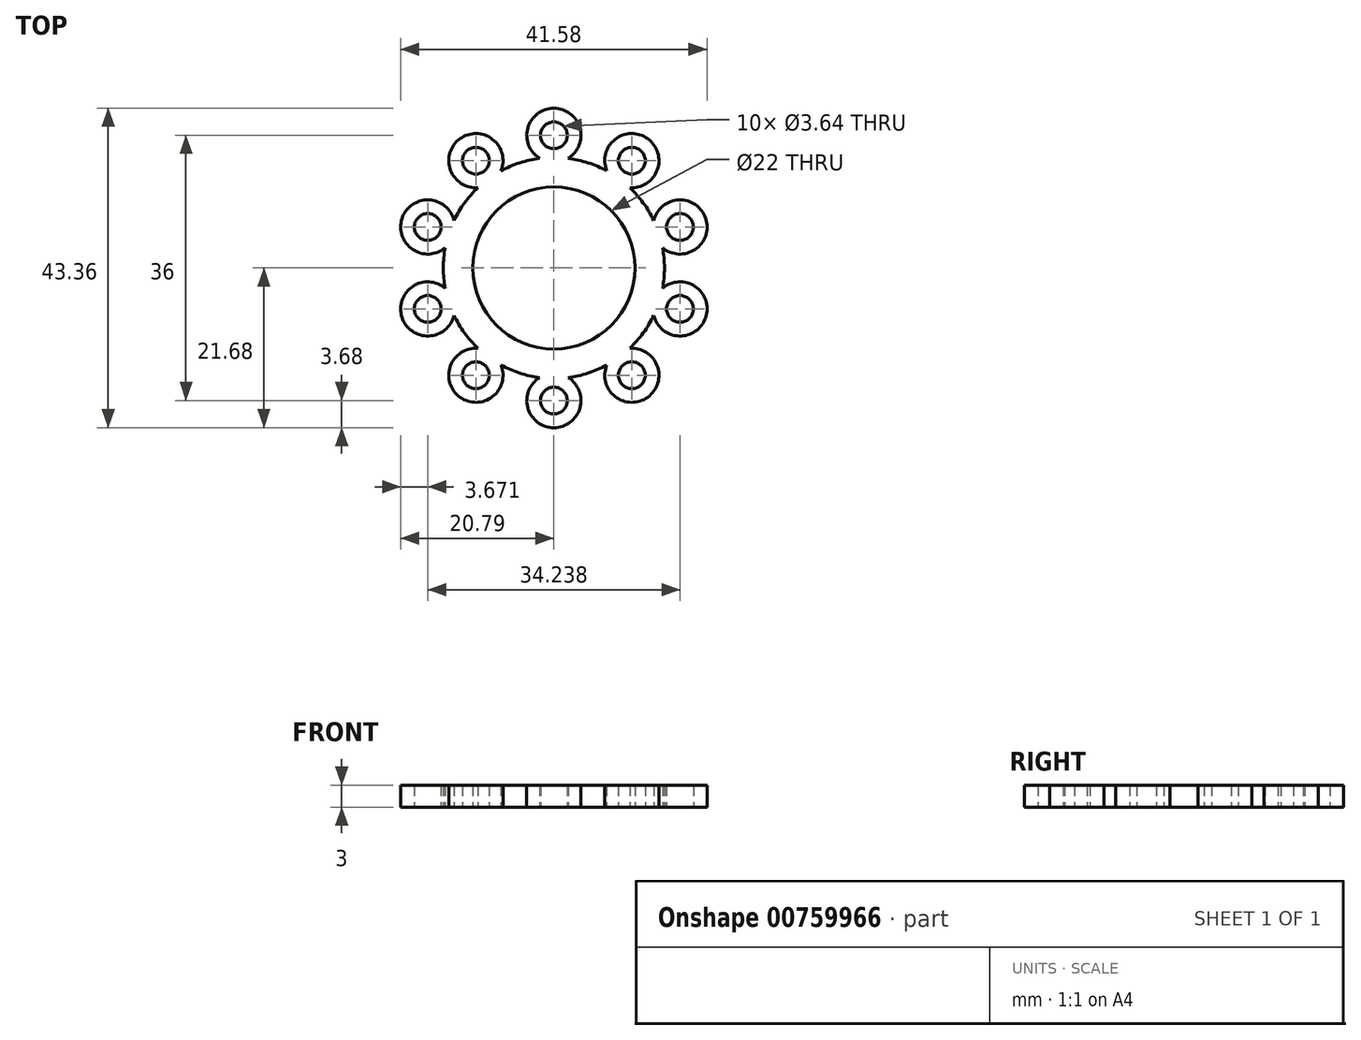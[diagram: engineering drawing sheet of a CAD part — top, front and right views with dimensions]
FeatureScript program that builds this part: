
annotation { "Feature Type Name" : "Feature", "Feature Type Description" : "" }
export const myFeature = defineFeature(function(context is Context, id is Id, definition is map)
    precondition{}
    {
        {
            var Q0;
            Q0=qCreatedBy(makeId("Top.planeOp"),FACE);
            var sketch = newSketch(context, id + "F0", { "sketchPlane" : qUnion([Q0])});
            skArc(sketch, "E0", {"start": v(3.4, 10.46) * mm, "mid": v(0, 11) * mm, "end": v(-3.4, 10.46) * mm});
            skArc(sketch, "E1", {"start": v(4.64, 14.27) * mm, "mid": v(3.3, 14.63) * mm, "end": v(1.93, 14.87) * mm});
            skLineSegment(sketch, "E2", {"start": v(0, 0) * mm, "end": v(0, 11) * mm});
            skCircle(sketch, "E3", {"center": v(0, 18) * mm, "radius": 1.82 * mm});
            skArc(sketch, "E4", {"start": v(1.93, 14.87) * mm, "mid": v(0, 21.68) * mm, "end": v(-1.93, 14.87) * mm});
            skLineSegment(sketch, "E5.trimOffspring", {"start": v(0, 14.32) * mm, "end": v(0, 18) * mm});
            skArc(sketch, "E6.trimOffspring", {"start": v(-1.93, 14.87) * mm, "mid": v(-3.3, 14.63) * mm, "end": v(-4.64, 14.27) * mm});
            skArc(sketch, "E7.1.0", {"start": v(-7.18, 13.17) * mm, "mid": v(-12.74, 17.54) * mm, "end": v(-10.3, 10.9) * mm});
            skCircle(sketch, "E7.1.1", {"center": v(-10.58, 14.56) * mm, "radius": 1.82 * mm});
            skArc(sketch, "E7.1.2", {"start": v(-4.64, 14.27) * mm, "mid": v(-5.93, 13.78) * mm, "end": v(-7.18, 13.17) * mm});
            skArc(sketch, "E7.1.3", {"start": v(-3.4, 10.46) * mm, "mid": v(-6.47, 8.9) * mm, "end": v(-8.9, 6.47) * mm});
            skArc(sketch, "E7.1.4", {"start": v(-10.3, 10.9) * mm, "mid": v(-11.27, 9.9) * mm, "end": v(-12.14, 8.82) * mm});
            skArc(sketch, "E7.2.0", {"start": v(-13.55, 6.44) * mm, "mid": v(-20.61, 6.7) * mm, "end": v(-14.74, 2.76) * mm});
            skCircle(sketch, "E7.2.1", {"center": v(-17.12, 5.56) * mm, "radius": 1.82 * mm});
            skArc(sketch, "E7.2.2", {"start": v(-12.14, 8.82) * mm, "mid": v(-12.9, 7.66) * mm, "end": v(-13.55, 6.44) * mm});
            skArc(sketch, "E7.2.3", {"start": v(-8.9, 6.47) * mm, "mid": v(-10.46, 3.4) * mm, "end": v(-11, 0) * mm});
            skArc(sketch, "E7.2.4", {"start": v(-14.74, 2.76) * mm, "mid": v(-14.94, 1.38) * mm, "end": v(-15, 0) * mm});
            skArc(sketch, "E7.3.0", {"start": v(-14.74, -2.76) * mm, "mid": v(-20.61, -6.7) * mm, "end": v(-13.55, -6.44) * mm});
            skCircle(sketch, "E7.3.1", {"center": v(-17.12, -5.56) * mm, "radius": 1.82 * mm});
            skArc(sketch, "E7.3.2", {"start": v(-15, 0) * mm, "mid": v(-14.94, -1.38) * mm, "end": v(-14.74, -2.76) * mm});
            skArc(sketch, "E7.3.3", {"start": v(-11, 0) * mm, "mid": v(-10.46, -3.4) * mm, "end": v(-8.9, -6.47) * mm});
            skArc(sketch, "E7.3.4", {"start": v(-13.55, -6.44) * mm, "mid": v(-12.9, -7.66) * mm, "end": v(-12.14, -8.82) * mm});
            skArc(sketch, "E7.4.0", {"start": v(-10.3, -10.9) * mm, "mid": v(-12.74, -17.54) * mm, "end": v(-7.18, -13.17) * mm});
            skCircle(sketch, "E7.4.1", {"center": v(-10.58, -14.56) * mm, "radius": 1.82 * mm});
            skArc(sketch, "E7.4.2", {"start": v(-12.14, -8.82) * mm, "mid": v(-11.27, -9.9) * mm, "end": v(-10.3, -10.9) * mm});
            skArc(sketch, "E7.4.3", {"start": v(-8.9, -6.47) * mm, "mid": v(-6.47, -8.9) * mm, "end": v(-3.4, -10.46) * mm});
            skArc(sketch, "E7.4.4", {"start": v(-7.18, -13.17) * mm, "mid": v(-5.93, -13.78) * mm, "end": v(-4.64, -14.27) * mm});
            skArc(sketch, "E7.5.0", {"start": v(-1.93, -14.87) * mm, "mid": v(0, -21.68) * mm, "end": v(1.93, -14.87) * mm});
            skCircle(sketch, "E7.5.1", {"center": v(0, -18) * mm, "radius": 1.82 * mm});
            skArc(sketch, "E7.5.2", {"start": v(-4.64, -14.27) * mm, "mid": v(-3.3, -14.63) * mm, "end": v(-1.93, -14.87) * mm});
            skArc(sketch, "E7.5.3", {"start": v(-3.4, -10.46) * mm, "mid": v(0, -11) * mm, "end": v(3.4, -10.46) * mm});
            skArc(sketch, "E7.5.4", {"start": v(1.93, -14.87) * mm, "mid": v(3.3, -14.63) * mm, "end": v(4.64, -14.27) * mm});
            skArc(sketch, "E7.6.0", {"start": v(7.18, -13.17) * mm, "mid": v(12.74, -17.54) * mm, "end": v(10.3, -10.9) * mm});
            skCircle(sketch, "E7.6.1", {"center": v(10.58, -14.56) * mm, "radius": 1.82 * mm});
            skArc(sketch, "E7.6.2", {"start": v(4.64, -14.27) * mm, "mid": v(5.93, -13.78) * mm, "end": v(7.18, -13.17) * mm});
            skArc(sketch, "E7.6.3", {"start": v(3.4, -10.46) * mm, "mid": v(6.47, -8.9) * mm, "end": v(8.9, -6.47) * mm});
            skArc(sketch, "E7.6.4", {"start": v(10.3, -10.9) * mm, "mid": v(11.27, -9.9) * mm, "end": v(12.14, -8.82) * mm});
            skArc(sketch, "E7.7.0", {"start": v(13.55, -6.44) * mm, "mid": v(20.61, -6.7) * mm, "end": v(14.74, -2.76) * mm});
            skCircle(sketch, "E7.7.1", {"center": v(17.12, -5.56) * mm, "radius": 1.82 * mm});
            skArc(sketch, "E7.7.2", {"start": v(12.14, -8.82) * mm, "mid": v(12.9, -7.66) * mm, "end": v(13.55, -6.44) * mm});
            skArc(sketch, "E7.7.3", {"start": v(8.9, -6.47) * mm, "mid": v(10.46, -3.4) * mm, "end": v(11, 0) * mm});
            skArc(sketch, "E7.7.4", {"start": v(14.74, -2.76) * mm, "mid": v(14.94, -1.38) * mm, "end": v(15, 0) * mm});
            skArc(sketch, "E7.8.0", {"start": v(14.74, 2.76) * mm, "mid": v(20.61, 6.7) * mm, "end": v(13.55, 6.44) * mm});
            skCircle(sketch, "E7.8.1", {"center": v(17.12, 5.56) * mm, "radius": 1.82 * mm});
            skArc(sketch, "E7.8.2", {"start": v(15, 0) * mm, "mid": v(14.94, 1.38) * mm, "end": v(14.74, 2.76) * mm});
            skArc(sketch, "E7.8.3", {"start": v(11, 0) * mm, "mid": v(10.46, 3.4) * mm, "end": v(8.9, 6.47) * mm});
            skArc(sketch, "E7.8.4", {"start": v(13.55, 6.44) * mm, "mid": v(12.9, 7.66) * mm, "end": v(12.14, 8.82) * mm});
            skArc(sketch, "E7.9.0", {"start": v(10.3, 10.9) * mm, "mid": v(12.74, 17.54) * mm, "end": v(7.18, 13.17) * mm});
            skCircle(sketch, "E7.9.1", {"center": v(10.58, 14.56) * mm, "radius": 1.82 * mm});
            skArc(sketch, "E7.9.2", {"start": v(12.14, 8.82) * mm, "mid": v(11.27, 9.9) * mm, "end": v(10.3, 10.9) * mm});
            skArc(sketch, "E7.9.3", {"start": v(8.9, 6.47) * mm, "mid": v(6.47, 8.9) * mm, "end": v(3.4, 10.46) * mm});
            skArc(sketch, "E7.9.4", {"start": v(7.18, 13.17) * mm, "mid": v(5.93, 13.78) * mm, "end": v(4.64, 14.27) * mm});
            skSolve(sketch);
        }
        {
            var Q0;
            Q0=makeQuery(id+"F0.imprint","IMPRINT",FACE,{"disambiguationData":[TD([[makeQuery(id+"F0.imprint","IMPRINT",EDGE,{"derivedFrom":sQuery(id+"F0.wireOp",EDGE,"E1")}),1.0]])]});
            extrude(context, id + "F1", {"entities" : qUnion([Q0]), "depth" : 3 * mm, "offsetDistance" : 25 * mm});
        }
    });
